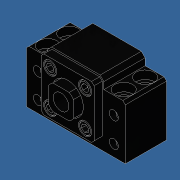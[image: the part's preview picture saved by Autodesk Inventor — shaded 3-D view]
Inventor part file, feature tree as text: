
AUTODESK INVENTOR PART (.ipt)
format: ipt  version: 2013 SP1 (Build 170176100, 176)  size: 368,128 bytes
history: native  units: in
note: dims shown in document units (in); Inventor stores cm internally (conversion verified against a paired STEP export)
features: sketch x12, projected_geometry x10, extrude x8, hole x4, chamfer x4, pattern_circular x1
ambient origin geometry x8: Origin, YZ Plane, XZ Plane, XY Plane, X Axis, Y Axis, Z Axis, Center Point
bodies: Solid1 (feature_tree)
feature tree (39):
  extrude  "Extrusion1"  Depth=1.5354in
  hole  "Hole1"  [1 undecoded]
  hole  "Hole2"  [1 undecoded]
  hole  "Hole3"  [1 undecoded]
  chamfer  "Chamfer1"  Distance=0.09in Angle=45.0deg
  chamfer  "Chamfer2"  Distance=0.06in Angle=45.0deg
  extrude  "Extrusion2"  Depth=1.2598in
  chamfer  "Chamfer3"  Distance=0.1969in
  hole  "Hole4"  [1 undecoded]
  extrude  "Extrusion3"  Depth=0.1181in TaperAngle=0.0deg
  extrude  "Extrusion4"  Depth=0.7087in
  extrude  "Extrusion5"  Depth=0.374in
  extrude  "Extrusion6"  Depth=0.4724in TaperAngle=0.0deg
  extrude  "Extrusion7"  Depth=0.5906in
  chamfer  "Chamfer4"  Distance=0.2362in
  pattern_circular  "Circular Pattern1"  [2 undecoded]
  extrude  "Extrusion8"  Depth=0.1575in TaperAngle=0.0deg
  sketch  "Sketch1"  dims[d0=2.3622in d1=1.5354in]
  sketch  "Sketch2"  dims[d2=1.3386in d3=1.2795in]
  projected_geometry  "Projected Loop1"
  sketch  "Sketch3"  dims[d4=0.9843in d5=0.0in d6=0.8661in]
  projected_geometry  "Projected Loop2"
  sketch  "Sketch4"  dims[d7=0.7874in d8=0.75in d9=0.8661in d10=0.9449in d11=0.5635in d12=1.0in d13=0.8108in d14=0.5906in]
  projected_geometry  "Projected Loop3"
  projected_geometry  "Projected Loop4"
  sketch  "Sketch5"  dims[d16=1.811in]
  projected_geometry  "Projected Loop5"
  sketch  "Sketch7"  dims[d17=0.2165in d18=0.75in d19=0.8661in d20=0.2362in d21=0.5635in d22=1.0in d23=0.8108in]
  projected_geometry  "Projected Loop7"
  sketch  "Sketch8"  dims[d24=1.811in]
  projected_geometry  "Projected Loop8"
  sketch  "Sketch9"  dims[d26=0.2598in d27=0.75in d28=0.4252in d29=0.1969in d30=0.5635in d31=1.0in d32=0.8108in d33=0.09in d34=0.125in d35=45.0deg d36=0.06in d37=0.125in d38=45.0deg]
  sketch  "Sketch10"  dims[d39=0.5118in d40=1.2598in]
  projected_geometry  "Projected Loop9"
  sketch  "Sketch11"  dims[d42=0.748in d43=0.1969in d44=0.0in]
  projected_geometry  "Projected Loop10"
  sketch  "Sketch12"  dims[d45=0.06in d46=0.125in d47=45.0deg d48=1.1811in]
  projected_geometry  "Projected Loop11"
  sketch  "Sketch13"  dims[d50=0.177in d51=0.75in d52=0.315in d53=0.157in d54=0.5635in d55=1.0in d56=0.8108in d57=0.1181in d58=0.0in d59=0.7087in d61=0.374in d62=0.4724in d63=0.0in d64=0.5906in d65=0.2362in d66=0.0in d67=0.2953in d70=0.1575in d71=0.0in d72=0.1575in d73=0.1181in d74=0.0in d75=0.02in d76=0.125in d77=45.0deg d78=1.5748in d79=360.0deg d81=0.562in d83=0.3937in d84=0.045in d85=0.0in]
note: 6 required parameter values undecoded (feature->parameter linkage not recoverable at this tier; creation-order binding heuristic only, values carry confidence <= 0.55)
